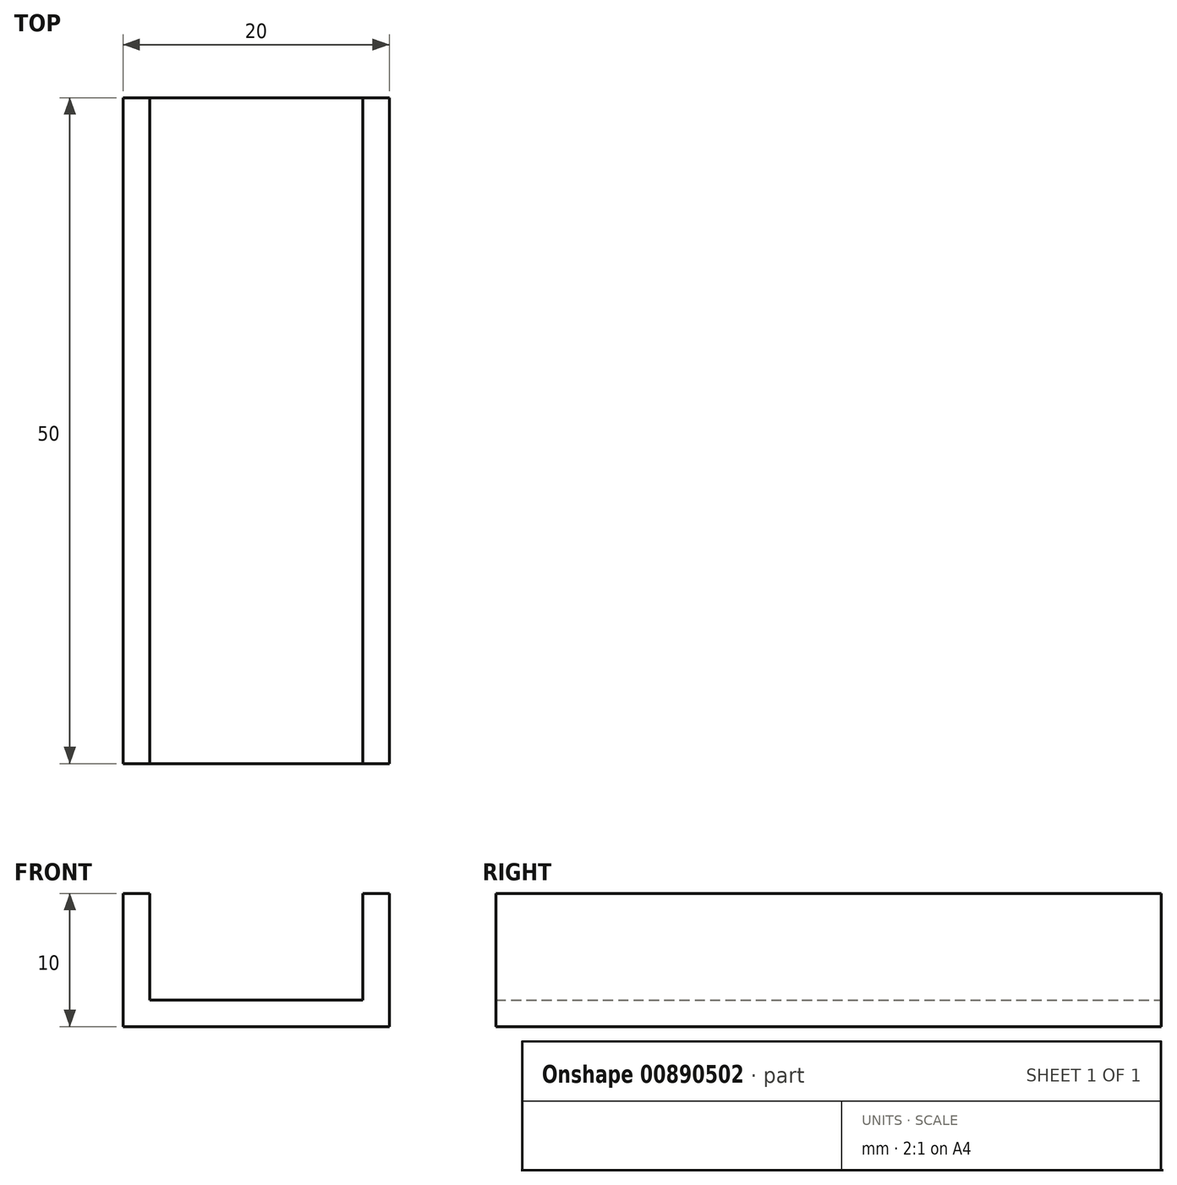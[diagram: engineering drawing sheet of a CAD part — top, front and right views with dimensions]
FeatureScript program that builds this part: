
annotation { "Feature Type Name" : "Feature", "Feature Type Description" : "" }
export const myFeature = defineFeature(function(context is Context, id is Id, definition is map)
    precondition{}
    {
        {
            var Q0;
            Q0=qCreatedBy(makeId("Front.planeOp"),FACE);
            var sketch = newSketch(context, id + "F0", { "sketchPlane" : qUnion([Q0])});
            skLineSegment(sketch, "E0.top", {"start": v(-6.1, -5.3) * mm, "end": v(13.9, -5.3) * mm});
            skLineSegment(sketch, "E0.left", {"start": v(-6.1, 4.7) * mm, "end": v(-6.1, -5.3) * mm});
            skLineSegment(sketch, "E0.right", {"start": v(13.9, 4.7) * mm, "end": v(13.9, -5.3) * mm});
            skPoint(sketch, "E1", {"position": v(13.9, -3.3) * mm});
            skPoint(sketch, "E2", {"position": v(-6.1, -3.3) * mm});
            skLineSegment(sketch, "E3", {"start": v(-4.1, 4.7) * mm, "end": v(-4.1, -5.3) * mm});
            skLineSegment(sketch, "E4", {"start": v(-6.1, -3.3) * mm, "end": v(13.9, -3.3) * mm});
            skLineSegment(sketch, "E5", {"start": v(11.9, 4.7) * mm, "end": v(11.9, -5.3) * mm});
            skPoint(sketch, "E6", {"position": v(-4.1, -3.3) * mm});
            skPoint(sketch, "E7", {"position": v(11.9, -3.3) * mm});
            skPoint(sketch, "E8", {"position": v(-4.1, 4.7) * mm});
            skPoint(sketch, "E9", {"position": v(11.9, 4.7) * mm});
            skPoint(sketch, "E10", {"position": v(13.9, 4.7) * mm});
            skPoint(sketch, "E11", {"position": v(-6.1, 4.7) * mm});
            skPoint(sketch, "E12", {"position": v(-6.1, -5.3) * mm});
            skPoint(sketch, "E13", {"position": v(-4.1, -5.3) * mm});
            skPoint(sketch, "E14", {"position": v(11.9, -5.3) * mm});
            skPoint(sketch, "E15", {"position": v(13.9, -5.3) * mm});
            skLineSegment(sketch, "E16", {"start": v(-6.1, 4.7) * mm, "end": v(-4.1, 4.7) * mm});
            skLineSegment(sketch, "E17", {"start": v(11.9, 4.7) * mm, "end": v(13.9, 4.7) * mm});
            skSolve(sketch);
        }
        {
            var Q0;
            Q0=qSketchRegion(id+"F0",true);
            extrude(context, id + "F1", {"entities" : qUnion([Q0]), "depth" : 50 * mm, "offsetDistance" : 25 * mm});
        }
    });
